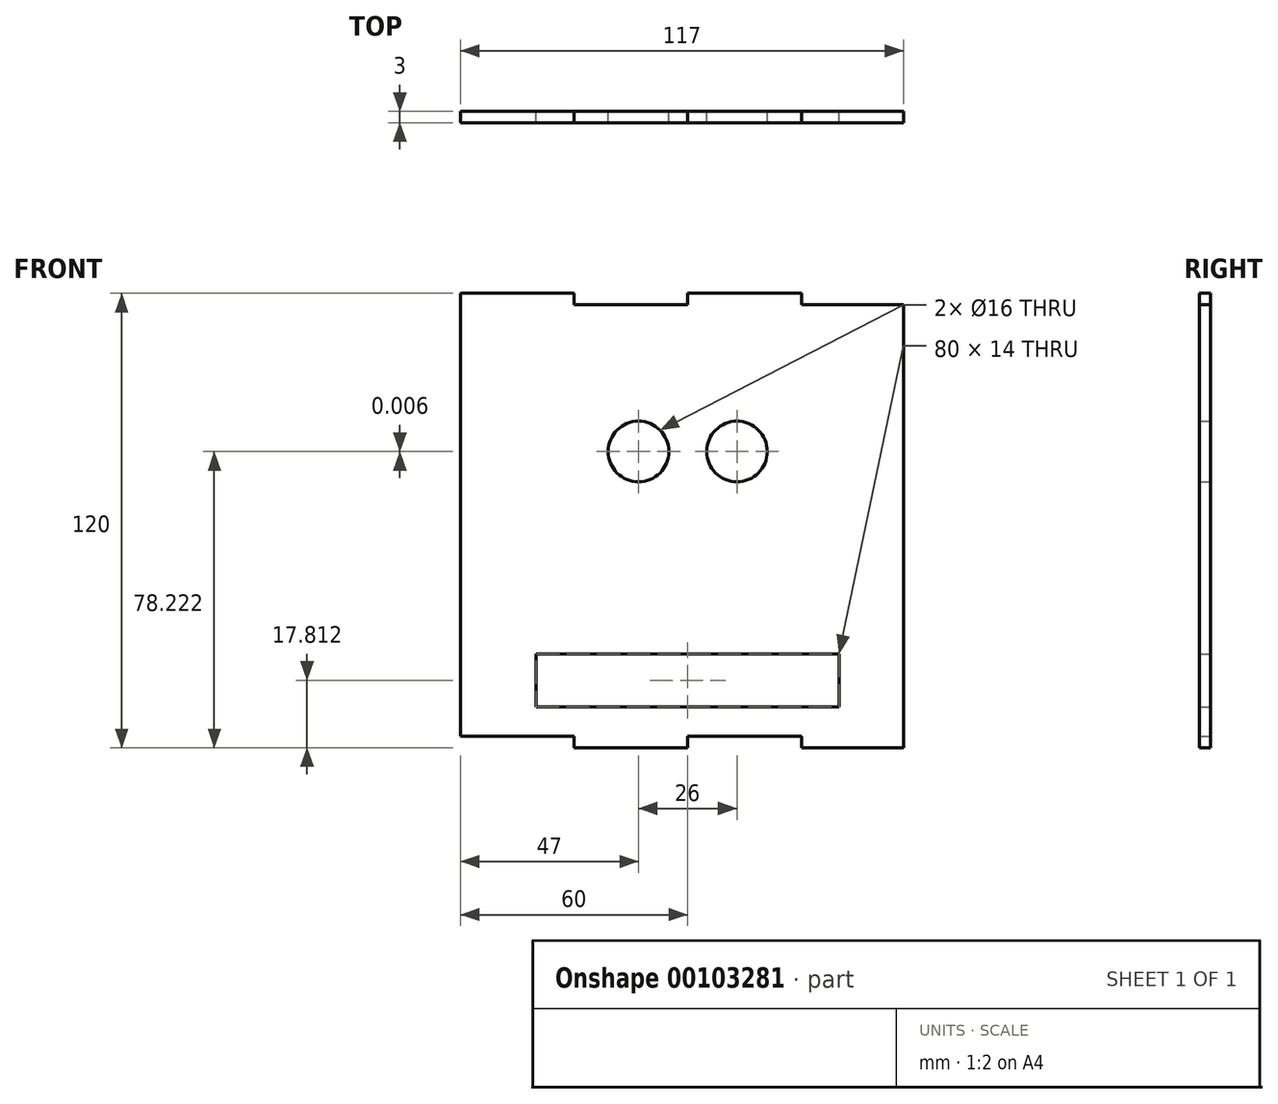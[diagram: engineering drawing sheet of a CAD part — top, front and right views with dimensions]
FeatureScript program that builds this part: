
annotation { "Feature Type Name" : "Feature", "Feature Type Description" : "" }
export const myFeature = defineFeature(function(context is Context, id is Id, definition is map)
    precondition{}
    {
        {
            var Q0;
            Q0=qCreatedBy(makeId("Front.planeOp"),FACE);
            var sketch = newSketch(context, id + "F0", { "sketchPlane" : qUnion([Q0])});
            skLineSegment(sketch, "E0", {"start": v(0, 0) * mm, "end": v(0, 0) * mm});
            skPoint(sketch, "E1.middle", {"position": v(0, 14.81) * mm});
            skPoint(sketch, "E2.middle", {"position": v(0, 75.23) * mm});
            skCircle(sketch, "E3", {"center": v(-13, 75.23) * mm, "radius": 8 * mm});
            skCircle(sketch, "E4.MirrorC", {"center": v(13, 75.22) * mm, "radius": 8 * mm});
            skLineSegment(sketch, "E5", {"start": v(0, 75.23) * mm, "end": v(0, 0) * mm, "construction": true});
            skLineSegment(sketch, "E6", {"start": v(-21, 74.98) * mm, "end": v(21, 75.22) * mm, "construction": true});
            skLineSegment(sketch, "E7", {"start": v(-5, 75.07) * mm, "end": v(5, 75.13) * mm, "construction": true});
            skLineSegment(sketch, "E8", {"start": v(0, 75.23) * mm, "end": v(0, 100) * mm, "construction": true});
            skLineSegment(sketch, "E9", {"start": v(0, 100) * mm, "end": v(0, -3) * mm, "construction": true});
            skLineSegment(sketch, "E10", {"start": v(0, -3) * mm, "end": v(-30, -3) * mm});
            skLineSegment(sketch, "E11", {"start": v(30, -3) * mm, "end": v(57, -3) * mm});
            skLineSegment(sketch, "E12", {"start": v(-60, 0) * mm, "end": v(-30, 0) * mm});
            skLineSegment(sketch, "E13", {"start": v(-30, 0) * mm, "end": v(-30, -3) * mm});
            skLineSegment(sketch, "E14", {"start": v(-30, -3) * mm, "end": v(0, -3) * mm});
            skLineSegment(sketch, "E15", {"start": v(0, -3) * mm, "end": v(0, 0) * mm});
            skLineSegment(sketch, "E16", {"start": v(0, 0) * mm, "end": v(30, 0) * mm});
            skLineSegment(sketch, "E17", {"start": v(30, 0) * mm, "end": v(30, -3) * mm});
            skLineSegment(sketch, "E18", {"start": v(57, -3) * mm, "end": v(57, 114) * mm});
            skLineSegment(sketch, "E19", {"start": v(30, 117) * mm, "end": v(0, 117) * mm});
            skLineSegment(sketch, "E20", {"start": v(-60, 117) * mm, "end": v(-60, 0) * mm});
            skLineSegment(sketch, "E21", {"start": v(-60, 117) * mm, "end": v(-30, 117) * mm});
            skLineSegment(sketch, "E22", {"start": v(-30, 117) * mm, "end": v(-30, 114) * mm});
            skLineSegment(sketch, "E23", {"start": v(-30, 114) * mm, "end": v(0, 114) * mm});
            skLineSegment(sketch, "E24", {"start": v(0, 114) * mm, "end": v(0, 117) * mm});
            skLineSegment(sketch, "E25", {"start": v(0, 117) * mm, "end": v(30, 117) * mm});
            skLineSegment(sketch, "E26", {"start": v(30, 117) * mm, "end": v(30, 114) * mm});
            skLineSegment(sketch, "E27", {"start": v(30, 114) * mm, "end": v(57, 114) * mm});
            skLineSegment(sketch, "E28.trimOffspring", {"start": v(-30, 117) * mm, "end": v(-60, 117) * mm});
            skLineSegment(sketch, "E29.bottom", {"start": v(40, 21.81) * mm, "end": v(-40, 21.81) * mm});
            skLineSegment(sketch, "E29.top", {"start": v(40, 7.81) * mm, "end": v(-40, 7.81) * mm});
            skLineSegment(sketch, "E29.left", {"start": v(40, 21.81) * mm, "end": v(40, 7.81) * mm});
            skLineSegment(sketch, "E29.right", {"start": v(-40, 21.81) * mm, "end": v(-40, 7.81) * mm});
            skSolve(sketch);
        }
        {
            var Q0;
            Q0=makeQuery(id+"F0.imprint","IMPRINT",FACE,{"disambiguationData":[TD([[makeQuery(id+"F0.imprint","IMPRINT",EDGE,{"derivedFrom":sQuery(id+"F0.wireOp",EDGE,"E1.bottom")}),1.0]])]});
            var Q1;
            Q1=makeQuery(id+"F0.imprint","IMPRINT",FACE,{"disambiguationData":[TD([[makeQuery(id+"F0.imprint","IMPRINT",EDGE,{"derivedFrom":sQuery(id+"F0.wireOp",EDGE,"E3")}),-1.0]])]});
            extrude(context, id + "F1", {"entities" : qUnion([Q0, Q1]), "endBound" : BoundingType.SYMMETRIC, "depth" : 3 * mm});
        }
    });
